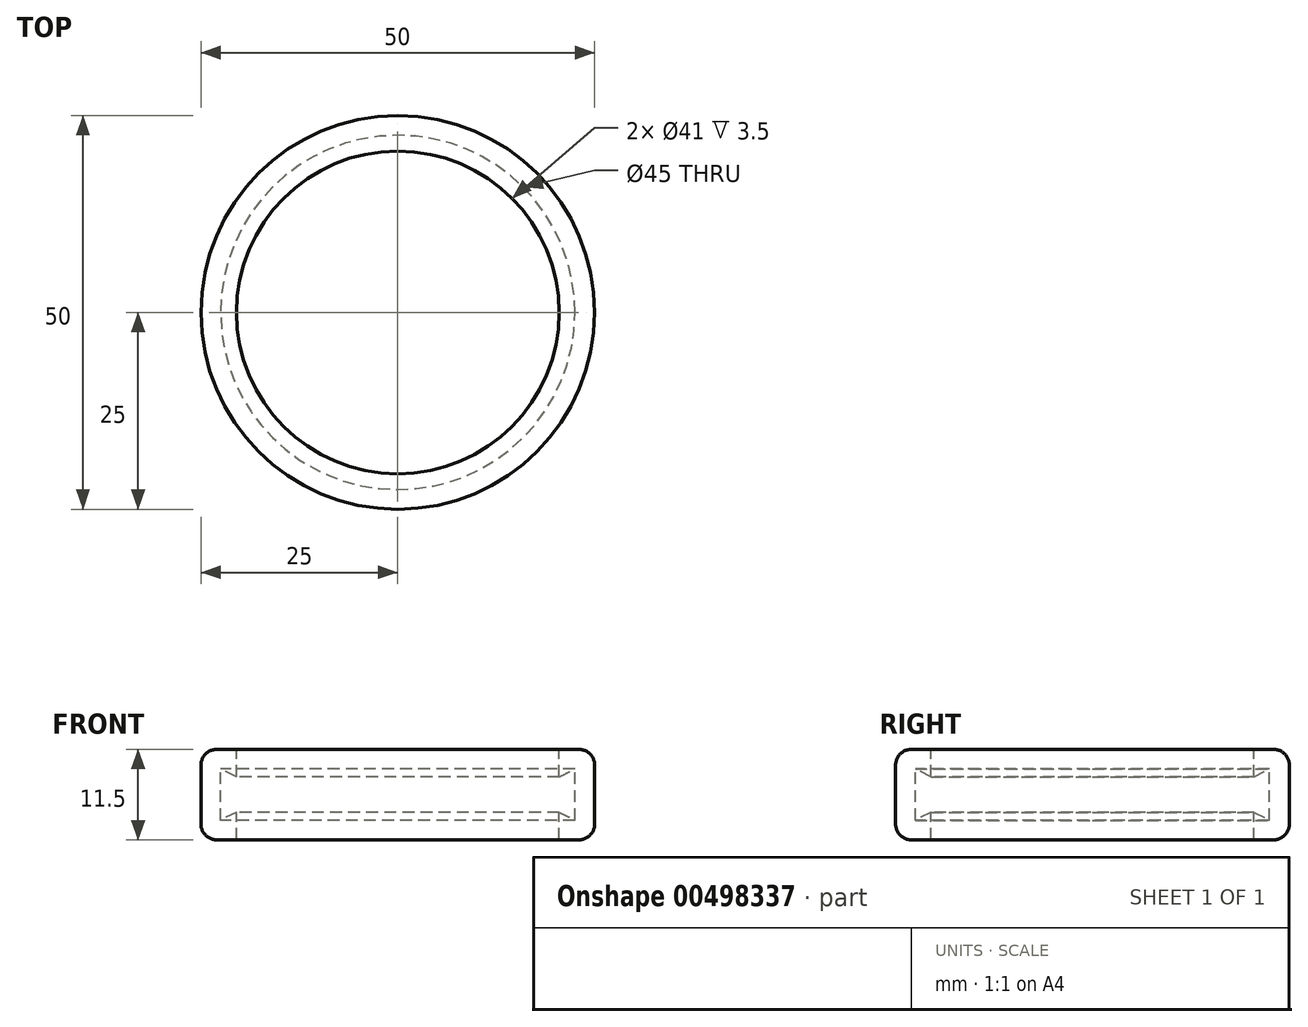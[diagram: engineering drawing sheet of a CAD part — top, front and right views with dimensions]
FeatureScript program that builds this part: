
annotation { "Feature Type Name" : "Feature", "Feature Type Description" : "" }
export const myFeature = defineFeature(function(context is Context, id is Id, definition is map)
    precondition{}
    {
        {
            var Q0;
            Q0=qCreatedBy(makeId("Front.planeOp"),FACE);
            var sketch = newSketch(context, id + "F0", { "sketchPlane" : qUnion([Q0])});
            skLineSegment(sketch, "E0", {"start": v(-22.5, -2.63) * mm, "end": v(-22.5, 3.87) * mm});
            skLineSegment(sketch, "E1", {"start": v(-22.5, 3.87) * mm, "end": v(-20.5, 2.87) * mm});
            skLineSegment(sketch, "E2", {"start": v(-20.5, 2.87) * mm, "end": v(-20.5, 6.37) * mm});
            skLineSegment(sketch, "E3", {"start": v(-20.5, 6.37) * mm, "end": v(-25, 6.37) * mm});
            skLineSegment(sketch, "E4", {"start": v(-25, 6.37) * mm, "end": v(-25, -5.13) * mm});
            skLineSegment(sketch, "E5", {"start": v(-25, -5.13) * mm, "end": v(-20.5, -5.13) * mm});
            skLineSegment(sketch, "E6", {"start": v(-20.5, -5.13) * mm, "end": v(-20.5, -1.63) * mm});
            skLineSegment(sketch, "E7", {"start": v(-20.5, -1.63) * mm, "end": v(-22.5, -2.63) * mm});
            skLineSegment(sketch, "E8", {"start": v(0, 9.88) * mm, "end": v(0, -8.42) * mm, "construction": true});
            skSolve(sketch);
        }
        {
            var Q0;
            Q0=makeQuery(id+"F0.imprint","IMPRINT",FACE,{"disambiguationData":[TD([[makeQuery(id+"F0.imprint","IMPRINT",EDGE,{"derivedFrom":sQuery(id+"F0.wireOp",EDGE,"E0")}),1.0]])]});
            var Q1;
            Q1=sQuery(id+"F0.wireOp",EDGE,"E8");
            revolve(context, id + "F1", {"entities" : qUnion([Q0]), "axis" : qUnion([Q1]), "revolveType" : RevolveType.FULL});
        }
        {
            var Q0;
            Q0=makeQuery(id+"F1.opRevolve","SWEPT_EDGE",EDGE,{"disambiguationData":[OSD([sQuery(id+"F0.wireOp",EDGE,"E3"),sQuery(id+"F0.wireOp",EDGE,"E4")])]});
            var Q1;
            Q1=makeQuery(id+"F1.opRevolve","SWEPT_FACE",FACE,{"disambiguationData":[OSD([sQuery(id+"F0.wireOp",EDGE,"E4")])]});
            fillet(context, id + "F2", {"entities" : qUnion([Q0, Q1]), "radius" : 2 * mm, "tangentPropagation" : true, "defaultsChanged" : false, "allowEdgeOverflow" : false, "vertexSettings" : [], "filletType" : FilletType.EDGE});
        }
    });
